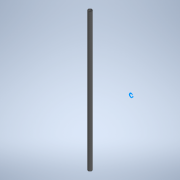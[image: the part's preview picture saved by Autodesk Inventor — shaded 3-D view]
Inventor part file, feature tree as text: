
AUTODESK INVENTOR PART (.ipt)
format: ipt  version: 2020 (Build 240168000, 168)  size: 95,744 bytes
history: native  units: mm
features: extrude x1, sketch x1
ambient origin geometry x8: Origin, YZ Plane, XZ Plane, XY Plane, X Axis, Y Axis, Z Axis, Center Point
bodies: Solid1 (feature_tree)
feature tree (2):
  extrude  "Extrusion1"  Depth=900.0mm
  sketch  "Sketch1"  dims[d0=25.0mm d1=21.0mm d2=900.0mm d3=0.0mm]
